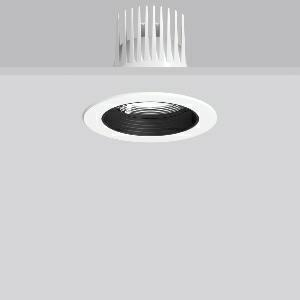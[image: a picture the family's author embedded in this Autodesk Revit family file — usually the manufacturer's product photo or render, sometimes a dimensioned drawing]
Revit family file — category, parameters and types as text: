
# Revit family: heledon_maxi_e_901762_002_3_4d12
name_source: partatom
category: Lighting Fixtures
units: mm (PartAtom-declared; Revit-internal decimal feet)

## family parameters
Cut with Voids When Loaded = No
Host = Face
Light Source = No
Part Type = Normal
Room Calculation Point = No
Round Connector Dimension = Use Diameter
Shared = No

## types (1)
- HELEDON maxi E (1 x LED Modul 935, 2850 lm, 3500)
    Apparent Load = 25 VA
    Approval mark = CE
    CIE Flux Codes = 96 100 100 100 100
    Color Rendering = 92
    Color Temperature = 3500
    Default Elevation = 1800 mm
    Description = Series: HELEDON maxi
Round recessed downlight. Housing: die-cast aluminium, powder-coated. Black plastic ring and recessed LED to prevent glare from the side. Optical assembly with lens made of plastic (polycarbonate) for the best homogeneous light distribution - can be changed without tools. Best colour rendering index Ra>90. Suitable for Recessed ceiling mounting. Installation without tools thanks to spring fastening system. Including separate LED converter with connecting cable 600 mm.High quality converter without flickering and stroboscopic effect. Through-wiring box (5 pole) available as accessory. The following accessories can be mounted without use of tools: interchangeable lenses, decorative glasses, honeycomb louvre, clear and frosted diffusers, white interchangeable plastic ring. 
Colour: traffic white, matt (RAL 9016)
Diameter: 162 mm
Height: 3 mm
Cut-out diameter: 152 mm
Recess height: 200 mm
Luminaire: recess height: 135 mm
Lamp: LED
Socket: without socket
Colour temperature: 3500K
Colour rendering index (CRI): 92
System power: 25 W
Rated luminous flux: 2850 lm
Luminous efficiency: 114 lm/W
Control gear: Regulated power supply
Protection class: II
Type of protection: IP 20
    Height = 0 mm  [stored 0 ft]
    Lamp = 1 x LED Modul 935
    Lamp Light Flux = 2850 lm
    Lamp count = 1
    Length = 162 mm
    Lifetime = 50000 h
    Luminous efficacy = 114 lm/W
    Manufacturer = RZB
    ModVariant = No
    Model = 901762.002.3
    Mounting Place = Ceiling
    Mounting Type = Recessed
    Number of Poles = 1
    OnlyDefault = Yes
    Power Factor = 1
    Product Name = HELEDON maxi E
    Product group = Recessed downlights
    ProductGroupID = 402
    Protection Class = Protection class II
    Protection Degree = IP 20
    RLX_Detail_Level = 1
    RLX_Emergency_Light_Flux = 0 lm
    RLX_Emergency_Type = 0
    RLX_Emergency_Type_DB = No
    RlxData = <blob elided: 119497 chars, md5=3ed76c5e>
    Socket = socket
    Standby Power = 0 W
    System Light Flux = 2850 lm
    System Power = 25 W
    Type Comments = Product without accessories
    Type Image = 901663.002.jpg
    URL = http://relux.com
    VarID = ---
    Voltage = 230 V
    Voltage Range = 220-240 V
    Weight = 0.00 kg
    Width = 0 mm  [stored 0 ft]

note: [stored X ft] marks values corroborated as IEEE doubles in the binary element streams (Revit-internal decimal feet)

## geometry (parser evidence)
native form markers: Blend x4, Sweep x11
no freeform markers — native parametric forms only
